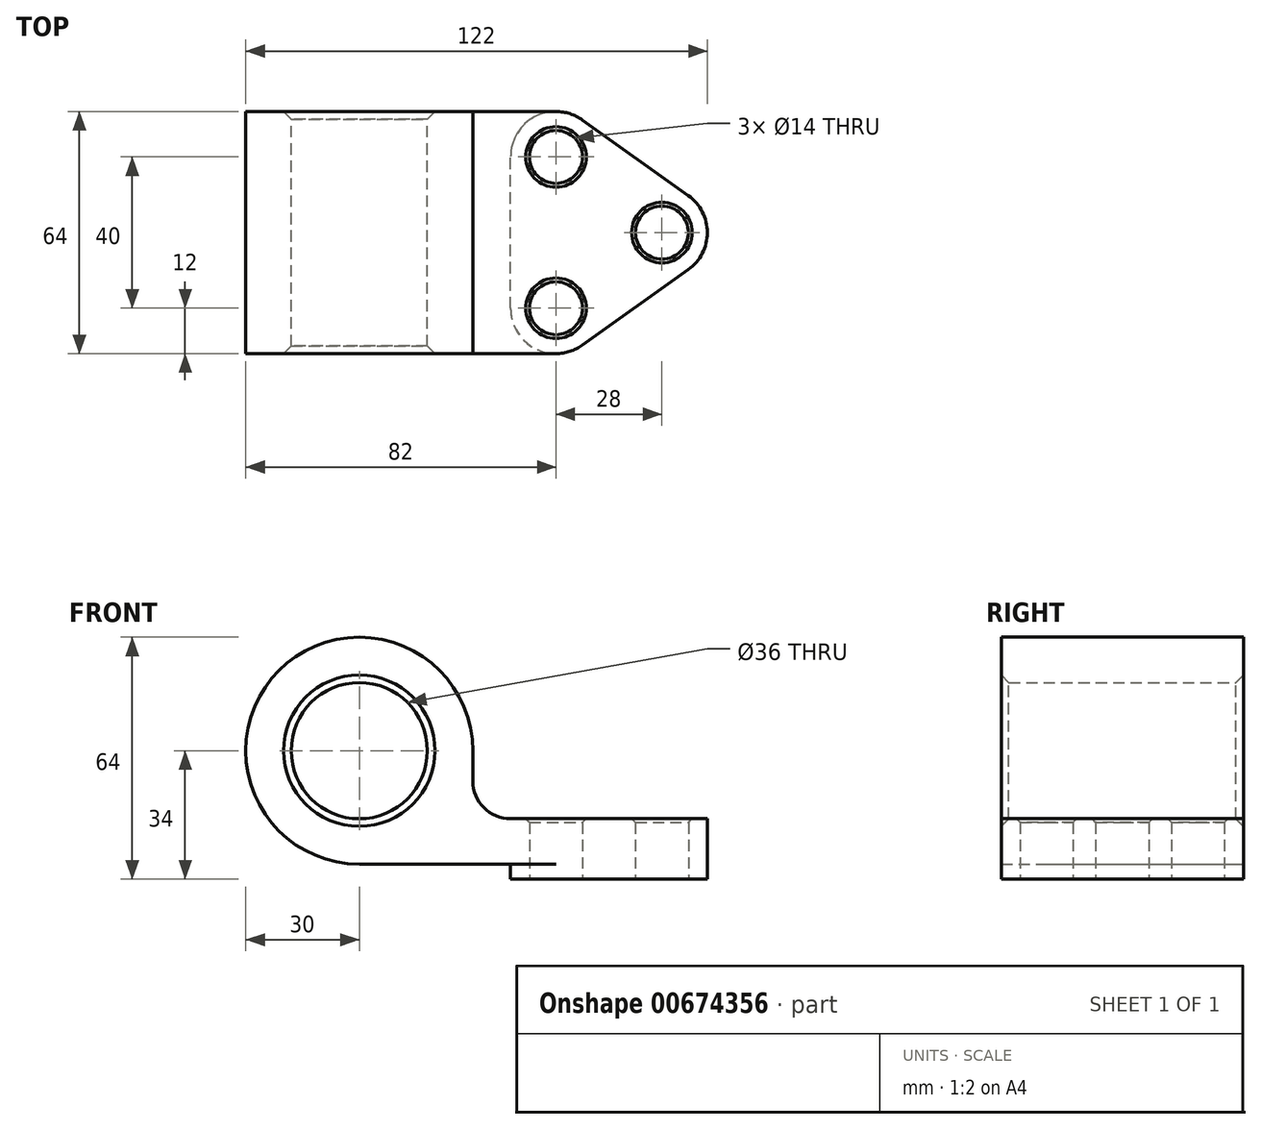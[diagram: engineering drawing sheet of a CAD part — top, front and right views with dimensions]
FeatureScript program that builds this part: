
annotation { "Feature Type Name" : "Feature", "Feature Type Description" : "" }
export const myFeature = defineFeature(function(context is Context, id is Id, definition is map)
    precondition{}
    {
        {
            var Q0;
            Q0=qCreatedBy(makeId("Front.planeOp"),FACE);
            var sketch = newSketch(context, id + "F0", { "sketchPlane" : qUnion([Q0])});
            skCircle(sketch, "E0", {"center": v(0, 0) * mm, "radius": 30 * mm});
            skCircle(sketch, "E1", {"center": v(0, 0) * mm, "radius": 18 * mm});
            skLineSegment(sketch, "E2", {"start": v(0, 0) * mm, "end": v(0, -30) * mm, "construction": true});
            skLineSegment(sketch, "E3", {"start": v(0, -30) * mm, "end": v(40, -30) * mm});
            skLineSegment(sketch, "E4", {"start": v(40, -30) * mm, "end": v(40, -34) * mm});
            skLineSegment(sketch, "E5", {"start": v(40, -34) * mm, "end": v(52, -34) * mm});
            skLineSegment(sketch, "E6", {"start": v(52, -34) * mm, "end": v(80, -34) * mm});
            skLineSegment(sketch, "E7", {"start": v(80, -34) * mm, "end": v(92, -34) * mm});
            skLineSegment(sketch, "E8", {"start": v(92, -34) * mm, "end": v(92, -18) * mm});
            skLineSegment(sketch, "E9", {"start": v(92, -18) * mm, "end": v(30, -18) * mm});
            skLineSegment(sketch, "E10", {"start": v(30, 0) * mm, "end": v(30, -18) * mm});
            skSolve(sketch);
        }
        {
            var Q0;
            Q0=makeQuery(id+"F0.imprint","IMPRINT",FACE,{"disambiguationData":[TD([[makeQuery(id+"F0.imprint","IMPRINT",EDGE,{"derivedFrom":sQuery(id+"F0.wireOp",EDGE,"E1")}),-1.0]])]});
            var Q1;
            {var subQ0=sQuery(id+"F0.wireOp",EDGE,"E3");Q1=makeQuery(id+"F0.imprint","IMPRINT",FACE,{"disambiguationData":[TD([[makeQuery(id+"F0.imprint","IMPRINT",EDGE,{"derivedFrom":subQ0}),1.0]])]});}
            extrude(context, id + "F1", {"entities" : qUnion([Q0, Q1]), "depth" : 64 * mm, "offsetDistance" : 25 * mm});
        }
        {
            var Q0;
            Q0=makeQuery(id+"F1.opExtrude","SWEPT_FACE",FACE,{"disambiguationData":[OSD([sQuery(id+"F0.wireOp",EDGE,"E5"),sQuery(id+"F0.wireOp",EDGE,"E6"),sQuery(id+"F0.wireOp",EDGE,"E7")])]});
            var sketch = newSketch(context, id + "F2", { "sketchPlane" : qUnion([Q0])});
            skLineSegment(sketch, "E11", {"start": v(40, 64) * mm, "end": v(52, 64) * mm, "construction": true});
            skLineSegment(sketch, "E12", {"start": v(52, 64) * mm, "end": v(52, 0) * mm, "construction": true});
            skLineSegment(sketch, "E13", {"start": v(52, 0) * mm, "end": v(80, 0) * mm, "construction": true});
            skLineSegment(sketch, "E14", {"start": v(80, 0) * mm, "end": v(80, 64) * mm, "construction": true});
            skLineSegment(sketch, "E15", {"start": v(52, 64) * mm, "end": v(52, 52) * mm, "construction": true});
            skCircle(sketch, "E16", {"center": v(80, 32) * mm, "radius": 7 * mm});
            skCircle(sketch, "E17", {"center": v(52, 52) * mm, "radius": 7 * mm});
            skLineSegment(sketch, "E18", {"start": v(52, 0) * mm, "end": v(52, 12) * mm, "construction": true});
            skCircle(sketch, "E19", {"center": v(52, 12) * mm, "radius": 7 * mm});
            skArc(sketch, "E20", {"start": v(58.97, 61.76) * mm, "mid": v(46.5, 62.67) * mm, "end": v(40, 52) * mm});
            skArc(sketch, "E21", {"start": v(86.97, 22.24) * mm, "mid": v(92, 32) * mm, "end": v(86.97, 41.76) * mm});
            skArc(sketch, "E22", {"start": v(40, 12) * mm, "mid": v(46.5, 1.33) * mm, "end": v(58.97, 2.24) * mm});
            skLineSegment(sketch, "E23", {"start": v(52, 52) * mm, "end": v(80, 32) * mm, "construction": true});
            skLineSegment(sketch, "E24", {"start": v(52, 12) * mm, "end": v(80, 32) * mm, "construction": true});
            skLineSegment(sketch, "E25", {"start": v(52, 52) * mm, "end": v(58.97, 61.76) * mm, "construction": true});
            skLineSegment(sketch, "E26", {"start": v(58.97, 61.76) * mm, "end": v(86.97, 41.76) * mm});
            skLineSegment(sketch, "E27", {"start": v(80, 32) * mm, "end": v(86.97, 22.24) * mm, "construction": true});
            skLineSegment(sketch, "E28", {"start": v(86.97, 22.24) * mm, "end": v(58.97, 2.24) * mm});
            skLineSegment(sketch, "E29", {"start": v(40, 52) * mm, "end": v(40, 12) * mm, "construction": true});
            skSolve(sketch);
        }
        {
            var Q0;
            {var subQ6=sQuery(id+"F2.wireOp",EDGE,"E26");Q0=makeQuery(id+"F2.imprint","IMPRINT",FACE,{"disambiguationData":[TD([[makeQuery(id+"F2.imprint","IMPRINT",EDGE,{"derivedFrom":subQ6}),1.0]])]});}
            var Q1;
            {var subQ6=sQuery(id+"F2.wireOp",EDGE,"E28");Q1=makeQuery(id+"F2.imprint","IMPRINT",FACE,{"disambiguationData":[TD([[makeQuery(id+"F2.imprint","IMPRINT",EDGE,{"derivedFrom":subQ6}),1.0]])]});}
            var Q2;
            Q2=makeQuery(id+"F2.imprint","IMPRINT",FACE,{"disambiguationData":[TD([[makeQuery(id+"F2.imprint","IMPRINT",EDGE,{"derivedFrom":sQuery(id+"F2.wireOp",EDGE,"E17")}),1.0]])]});
            var Q3;
            Q3=makeQuery(id+"F2.imprint","IMPRINT",FACE,{"disambiguationData":[TD([[makeQuery(id+"F2.imprint","IMPRINT",EDGE,{"derivedFrom":sQuery(id+"F2.wireOp",EDGE,"E19")}),1.0]])]});
            var Q4;
            Q4=makeQuery(id+"F2.imprint","IMPRINT",FACE,{"disambiguationData":[TD([[makeQuery(id+"F2.imprint","IMPRINT",EDGE,{"derivedFrom":sQuery(id+"F2.wireOp",EDGE,"E16")}),1.0]])]});
            extrude(context, id + "F3", {"entities" : qUnion([Q0, Q1, Q2, Q3, Q4]), "operationType" : NewBodyOperationType.REMOVE, "oppositeDirection" : true, "depth" : 25 * mm, "offsetDistance" : 25 * mm});
        }
        {
            var Q0;
            {var subQ0=sQuery(id+"F2.wireOp",EDGE,"E20");var subQ1=sQuery(id+"F0.wireOp",EDGE,"E5");var subQ2=makeQuery(id+"F1.opExtrude","SWEPT_EDGE",EDGE,{"disambiguationData":[OSD([sQuery(id+"F0.wireOp",EDGE,"E4"),subQ1])]});var subQ3=makeQuery(id+"F2.imprint","INTERSECT",VERTEX,{"derivedFrom":[subQ2,subQ0]});Q0=makeQuery(id+"F2.imprint","IMPRINT",FACE,{"disambiguationData":[TD([[makeQuery(id+"F2.imprint","IMPRINT",EDGE,{"disambiguationData":[TD([[subQ3,1.0]])],"derivedFrom":subQ0}),-1.0]])]});}
            var Q1;
            {var subQ0=sQuery(id+"F2.wireOp",EDGE,"E22");var subQ1=sQuery(id+"F0.wireOp",EDGE,"E5");var subQ2=makeQuery(id+"F1.opExtrude","SWEPT_EDGE",EDGE,{"disambiguationData":[OSD([sQuery(id+"F0.wireOp",EDGE,"E4"),subQ1])]});var subQ3=makeQuery(id+"F2.imprint","INTERSECT",VERTEX,{"derivedFrom":[subQ2,subQ0]});Q1=makeQuery(id+"F2.imprint","IMPRINT",FACE,{"disambiguationData":[TD([[makeQuery(id+"F2.imprint","IMPRINT",EDGE,{"disambiguationData":[TD([[subQ3,-1.0]])],"derivedFrom":subQ0}),-1.0]])]});}
            extrude(context, id + "F4", {"entities" : qUnion([Q0, Q1]), "operationType" : NewBodyOperationType.REMOVE, "oppositeDirection" : true, "depth" : 4 * mm, "offsetDistance" : 25 * mm});
        }
        {
            var Q0;
            Q0=makeQuery(id+"F3.boolean.opBoolean","INTERSECT",EDGE,{"derivedFrom":[makeQuery(id+"F1.opExtrude","SWEPT_FACE",FACE,{"disambiguationData":[OSD([sQuery(id+"F0.wireOp",EDGE,"E9")])]}),makeQuery(id+"F3.opExtrude","SWEPT_FACE",FACE,{"disambiguationData":[OSD([sQuery(id+"F2.wireOp",EDGE,"E19")])]})]});
            var Q1;
            Q1=makeQuery(id+"F3.boolean.opBoolean","INTERSECT",EDGE,{"derivedFrom":[makeQuery(id+"F1.opExtrude","SWEPT_FACE",FACE,{"disambiguationData":[OSD([sQuery(id+"F0.wireOp",EDGE,"E9")])]}),makeQuery(id+"F3.opExtrude","SWEPT_FACE",FACE,{"disambiguationData":[OSD([sQuery(id+"F2.wireOp",EDGE,"E16")])]})]});
            var Q2;
            Q2=makeQuery(id+"F3.boolean.opBoolean","INTERSECT",EDGE,{"derivedFrom":[makeQuery(id+"F1.opExtrude","SWEPT_FACE",FACE,{"disambiguationData":[OSD([sQuery(id+"F0.wireOp",EDGE,"E9")])]}),makeQuery(id+"F3.opExtrude","SWEPT_FACE",FACE,{"disambiguationData":[OSD([sQuery(id+"F2.wireOp",EDGE,"E17")])]})]});
            var Q3;
            Q3=makeQuery(id+"F3.boolean.opBoolean","COPY",EDGE,{"derivedFrom":makeQuery(id+"F3.opExtrude","CAP_EDGE",EDGE,{"disambiguationData":[OSD([sQuery(id+"F2.wireOp",EDGE,"E17")])],"isStart":true})});
            var Q4;
            Q4=makeQuery(id+"F3.boolean.opBoolean","COPY",EDGE,{"derivedFrom":makeQuery(id+"F3.opExtrude","CAP_EDGE",EDGE,{"disambiguationData":[OSD([sQuery(id+"F2.wireOp",EDGE,"E16")])],"isStart":true})});
            var Q5;
            Q5=makeQuery(id+"F3.boolean.opBoolean","COPY",EDGE,{"derivedFrom":makeQuery(id+"F3.opExtrude","CAP_EDGE",EDGE,{"disambiguationData":[OSD([sQuery(id+"F2.wireOp",EDGE,"E19")])],"isStart":true})});
            chamfer(context, id + "F5", {"entities" : qUnion([Q0, Q1, Q2, Q3, Q4, Q5]), "chamferType" : ChamferType.OFFSET_ANGLE, "width" : 1 * mm, "oppositeDirection" : false, "angle" : 45 * degree, "tangentPropagation" : true});
        }
        {
            var Q0;
            Q0=makeQuery(id+"F1.opExtrude","CAP_EDGE",EDGE,{"disambiguationData":[OSD([sQuery(id+"F0.wireOp",EDGE,"E1")])],"isStart":true});
            var Q1;
            Q1=makeQuery(id+"F1.opExtrude","CAP_EDGE",EDGE,{"disambiguationData":[OSD([sQuery(id+"F0.wireOp",EDGE,"E1")])],"isStart":false});
            chamfer(context, id + "F6", {"entities" : qUnion([Q0, Q1]), "chamferType" : ChamferType.OFFSET_ANGLE, "width" : 2 * mm, "oppositeDirection" : false, "angle" : 45 * degree, "tangentPropagation" : true});
        }
        {
            var Q0;
            Q0=makeQuery(id+"F1.opExtrude","SWEPT_EDGE",EDGE,{"disambiguationData":[OSD([sQuery(id+"F0.wireOp",EDGE,"E9"),sQuery(id+"F0.wireOp",EDGE,"E10")])]});
            fillet(context, id + "F7", {"entities" : qUnion([Q0]), "radius" : 10 * mm, "tangentPropagation" : true, "allowEdgeOverflow" : false});
        }
    });
